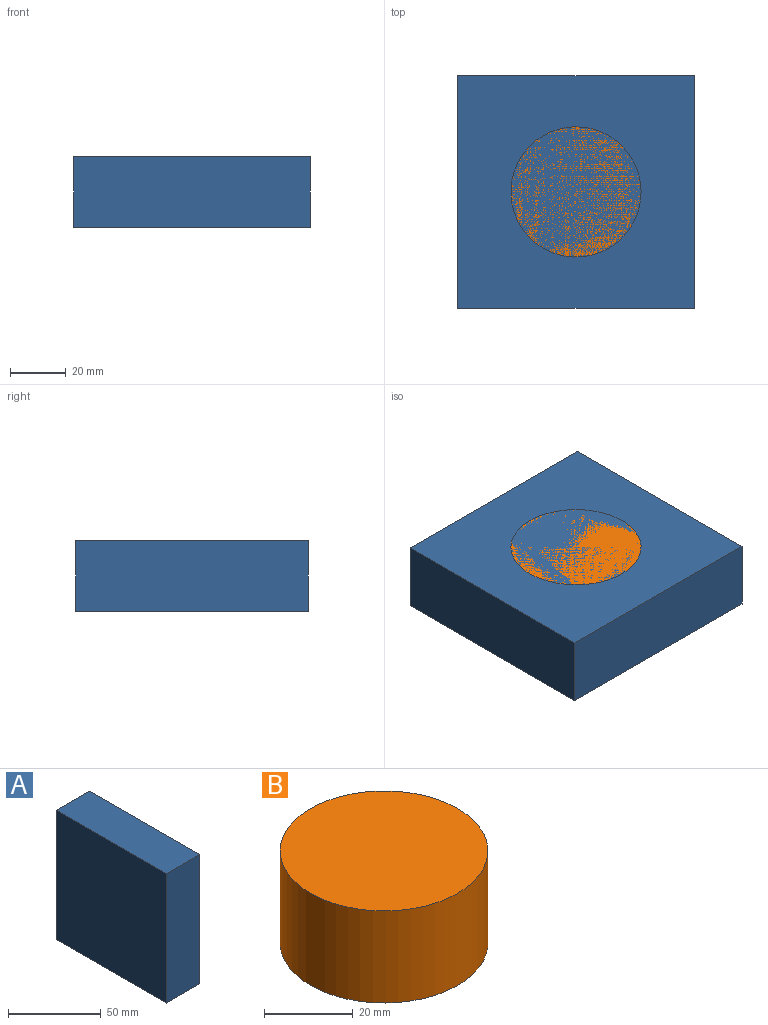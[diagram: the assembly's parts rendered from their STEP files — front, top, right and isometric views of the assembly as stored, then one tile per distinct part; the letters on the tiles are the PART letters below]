
ASSEMBLY  parts=2 mates=1
PART A: 6 faces, bbox 25.4x83.8x85.2 mm
  f0: plane 83.76x25.4mm, normal (0,0,1), area 2127.6mm2, adj f1,f3,f4,f5
  f1: plane 85.18x25.4mm, normal (0,-1,0), area 2163.6mm2, adj f0,f2,f4,f5
  f2: plane 83.76x25.4mm, normal (0,0,-1), area 2127.6mm2, adj f1,f3,f4,f5
  f3: plane 85.18x25.4mm, normal (0,1,0), area 2163.6mm2, adj f0,f2,f4,f5
  f4: plane 85.18x83.76mm, normal (1,0,0), area 7134.9mm2, adj f0,f1,f2,f3
  f5: plane 85.18x83.76mm, normal (-1,0,0), area 7134.9mm2, adj f0,f1,f2,f3
PART B: 3 faces, bbox 46.9x46.9x25.4 mm
  f0: cylinder r=23.43mm len=46.86mm, axis (0,0,-1), area 3739mm2, adj f1,f2
  f1: plane 46.86x46.86mm, normal (0,0,1), area 1724.3mm2, adj f0
  f2: plane 46.86x46.86mm, normal (0,0,-1), area 1724.3mm2, adj f0
PLACE A rot(axis=(0.71,0,0.71),180deg) t=(-10.17,22.82,-3)mm
PLACE B t=(21.59,5.78,-3)mm
MATE fastened A.f4 <-> B.f0  axis (0,0,1) through (-29.66,5.78,22.4)mm
